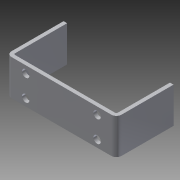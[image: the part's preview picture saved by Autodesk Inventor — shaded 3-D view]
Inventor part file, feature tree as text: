
AUTODESK INVENTOR PART (.ipt)
format: ipt  version: 2013 (Build 170138000, 138)  size: 115,712 bytes
history: native  units: in
note: dims shown in document units (in); Inventor stores cm internally (conversion verified against a paired STEP export)
features: sheet_metal_op x4, sketch x2, other x2
ambient origin geometry x8: Origin, YZ Plane, XZ Plane, XY Plane, X Axis, Y Axis, Z Axis, Center Point
feature tree (8):
  sheet_metal_op  "Face1"
  sheet_metal_op  "Flange1"
  sketch  "Sketch1"  dims[d0=3.5in]
  other  "Plate1"
  sketch  "Sketch2"  dims[d2=1.25in d3=0.7874in d5=2.5in d6=0.7874in d8=0.75in d11=0.25in d12=0.26in d15=0.125in d16=0.125in d17=0.0625in d18=0.25in d19=0.125in d20=2.0in d21=90.0deg d22=0.05in d23=0.5in d24=0.125in d25=0.125in]
  other  "Plate2"
  sheet_metal_op  "Bend1"
  sheet_metal_op  "Corner1"
